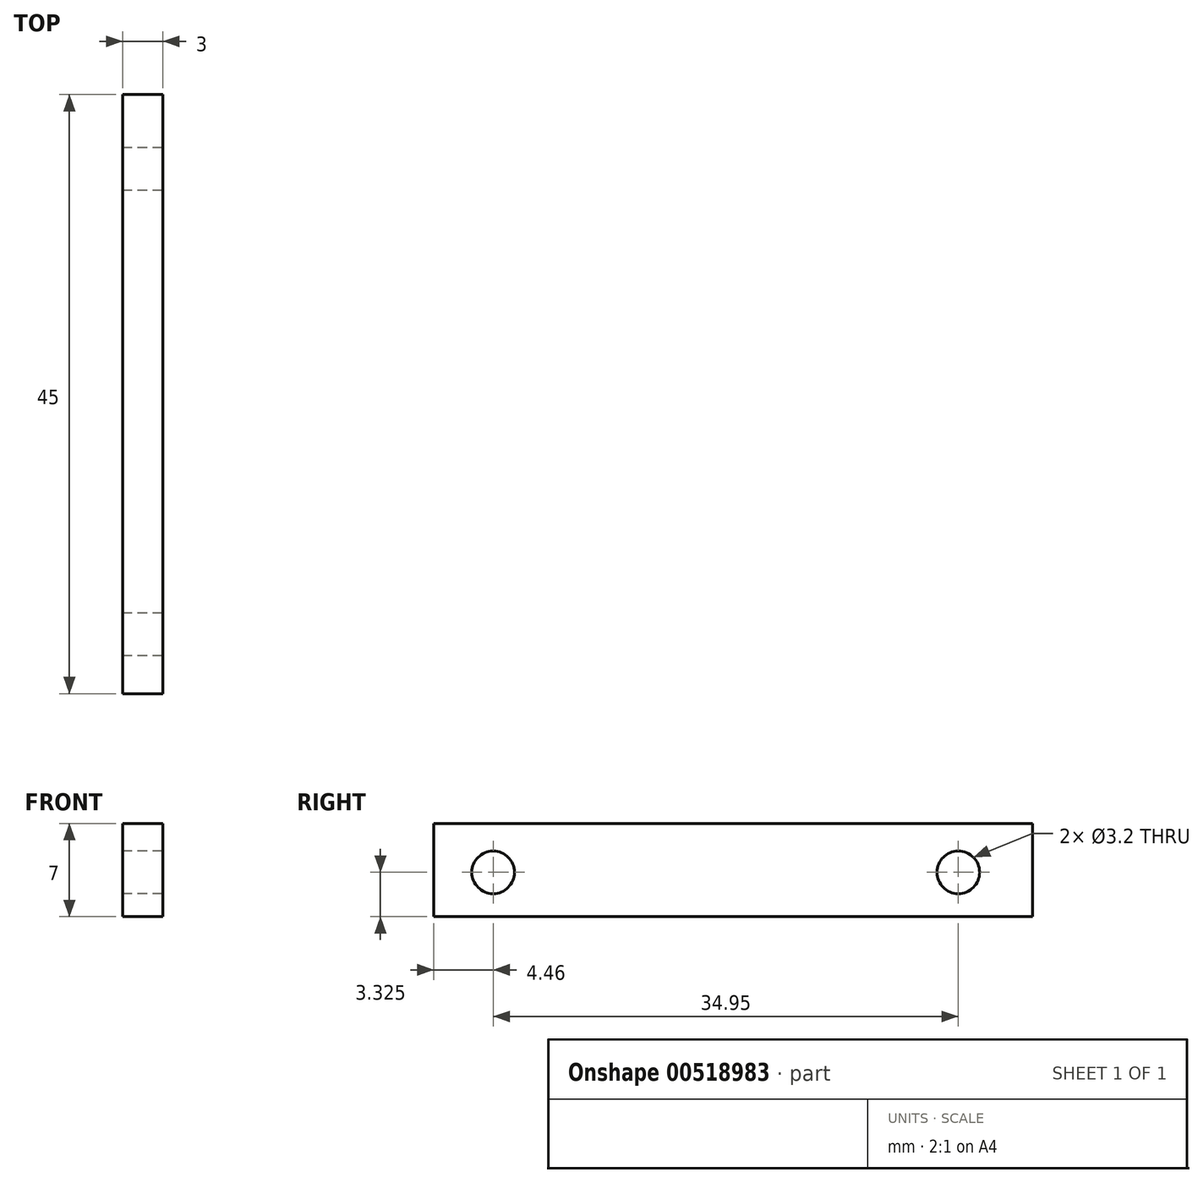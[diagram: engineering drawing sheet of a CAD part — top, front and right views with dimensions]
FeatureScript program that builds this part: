
annotation { "Feature Type Name" : "Feature", "Feature Type Description" : "" }
export const myFeature = defineFeature(function(context is Context, id is Id, definition is map)
    precondition{}
    {
        {
            var Q0;
            Q0=qCreatedBy(makeId("Right.planeOp"),FACE);
            var sketch = newSketch(context, id + "F0", { "sketchPlane" : qUnion([Q0])});
            skLineSegment(sketch, "E0.bottom", {"start": v(1.25, 4.33) * mm, "end": v(-43.75, 4.33) * mm});
            skLineSegment(sketch, "E0.top", {"start": v(1.25, 11.33) * mm, "end": v(-43.75, 11.33) * mm});
            skLineSegment(sketch, "E0.left", {"start": v(1.25, 4.33) * mm, "end": v(1.25, 11.33) * mm});
            skLineSegment(sketch, "E0.right", {"start": v(-43.75, 4.33) * mm, "end": v(-43.75, 11.33) * mm});
            skPoint(sketch, "E0.middle", {"position": v(-21.25, 7.83) * mm});
            skCircle(sketch, "E1", {"center": v(-39.29, 7.66) * mm, "radius": 1.6 * mm});
            skCircle(sketch, "E2", {"center": v(-4.34, 7.66) * mm, "radius": 1.6 * mm});
            skSolve(sketch);
        }
        {
            var Q0;
            Q0=makeQuery(id+"F0.imprint","IMPRINT",FACE,{"disambiguationData":[TD([[makeQuery(id+"F0.imprint","IMPRINT",EDGE,{"derivedFrom":sQuery(id+"F0.wireOp",EDGE,"E0.bottom")}),-1.0]])]});
            extrude(context, id + "F1", {"entities" : qUnion([Q0]), "depth" : 3 * mm, "offsetDistance" : 25 * mm});
        }
    });
